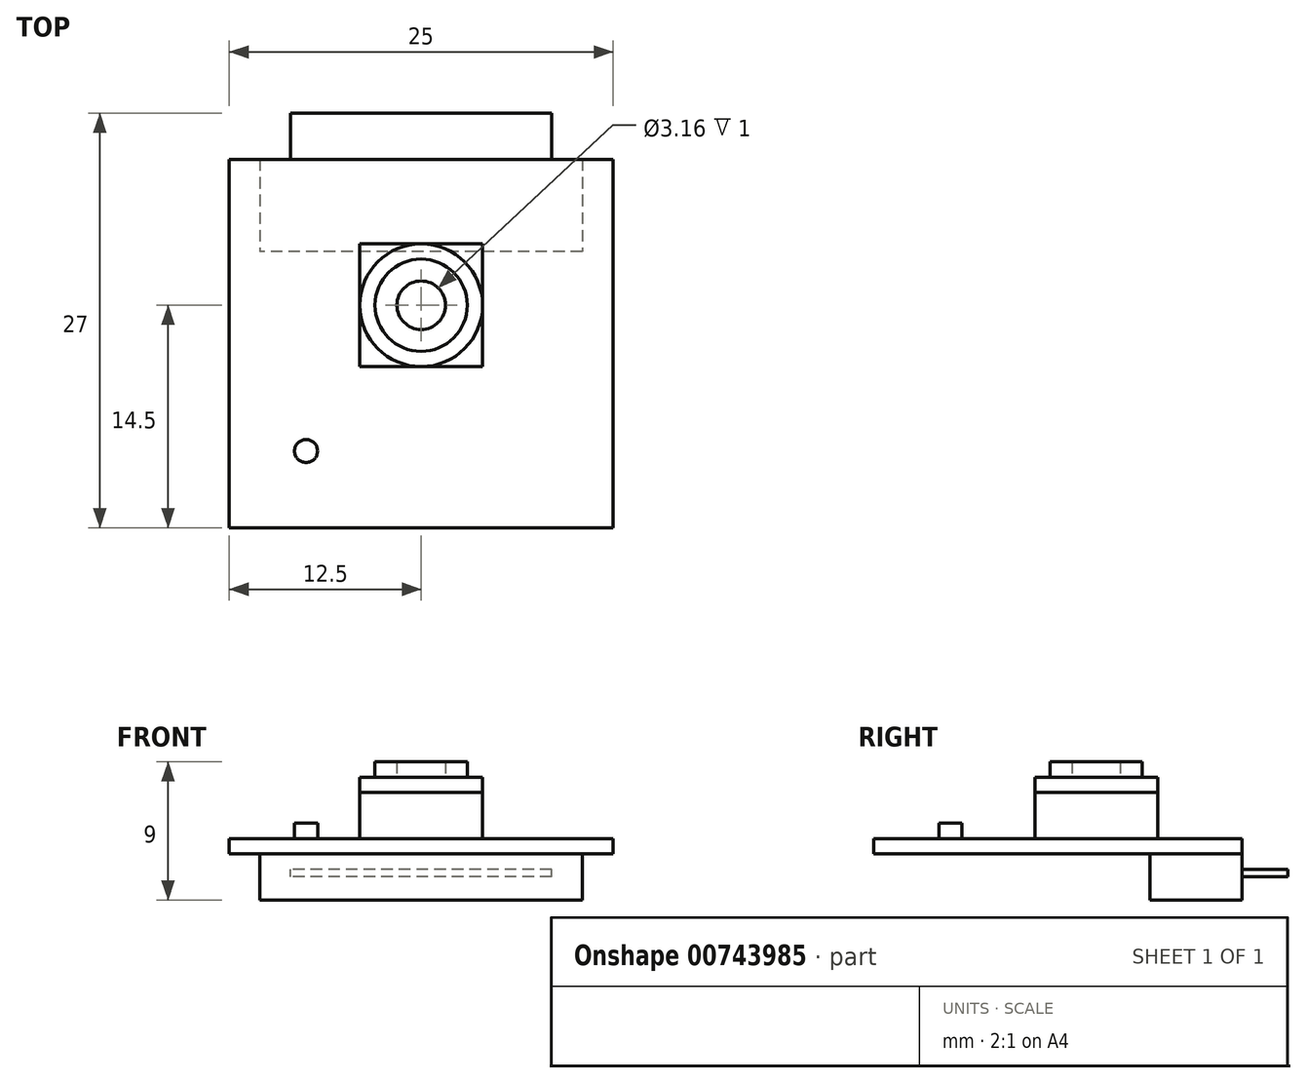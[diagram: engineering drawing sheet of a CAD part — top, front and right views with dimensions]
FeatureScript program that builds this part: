
annotation { "Feature Type Name" : "Feature", "Feature Type Description" : "" }
export const myFeature = defineFeature(function(context is Context, id is Id, definition is map)
    precondition{}
    {
        {
            var Q0;
            Q0=qCreatedBy(makeId("Top.planeOp"),FACE);
            var sketch = newSketch(context, id + "F0", { "sketchPlane" : qUnion([Q0])});
            skLineSegment(sketch, "E0", {"start": v(0, 11.87) * mm, "end": v(0, -10.8) * mm, "construction": true});
            skLineSegment(sketch, "E1", {"start": v(-15.08, 0) * mm, "end": v(17.29, 0) * mm, "construction": true});
            skLineSegment(sketch, "E2.bottom", {"start": v(-12.5, 12) * mm, "end": v(12.5, 12) * mm});
            skLineSegment(sketch, "E2.top", {"start": v(-12.5, -12) * mm, "end": v(12.5, -12) * mm});
            skLineSegment(sketch, "E2.left", {"start": v(-12.5, 12) * mm, "end": v(-12.5, -12) * mm});
            skLineSegment(sketch, "E2.right", {"start": v(12.5, 12) * mm, "end": v(12.5, -12) * mm});
            skSolve(sketch);
        }
        {
            var Q0;
            Q0=makeQuery(id+"F0.imprint","IMPRINT",FACE,{"disambiguationData":[TD([[makeQuery(id+"F0.imprint","IMPRINT",EDGE,{"derivedFrom":sQuery(id+"F0.wireOp",EDGE,"E2.bottom")}),-1.0]])]});
            extrude(context, id + "F1", {"entities" : qUnion([Q0]), "depth" : 1 * mm, "offsetDistance" : 25 * mm});
        }
        {
            var Q0;
            Q0=makeQuery(id+"F1.opExtrude","CAP_FACE",FACE,{"disambiguationData":[OSD([sQuery(id+"F0.wireOp",EDGE,"E2.bottom"),sQuery(id+"F0.wireOp",EDGE,"E2.top"),sQuery(id+"F0.wireOp",EDGE,"E2.left"),sQuery(id+"F0.wireOp",EDGE,"E2.right")])],"isStart":false});
            var sketch = newSketch(context, id + "F2", { "sketchPlane" : qUnion([Q0])});
            skLineSegment(sketch, "E3", {"start": v(0, 13.16) * mm, "end": v(0, -11.99) * mm, "construction": true});
            skLineSegment(sketch, "E4", {"start": v(-18.25, 0) * mm, "end": v(20.47, 0) * mm, "construction": true});
            skLineSegment(sketch, "E5.bottom", {"start": v(-4, 6.5) * mm, "end": v(4, 6.5) * mm});
            skLineSegment(sketch, "E5.top", {"start": v(-4, -1.5) * mm, "end": v(4, -1.5) * mm});
            skLineSegment(sketch, "E5.left", {"start": v(-4, 6.5) * mm, "end": v(-4, -1.5) * mm});
            skLineSegment(sketch, "E5.right", {"start": v(4, 6.5) * mm, "end": v(4, -1.5) * mm});
            skPoint(sketch, "E6", {"position": v(-7.5, -7) * mm});
            skCircle(sketch, "E7", {"center": v(-7.5, -7) * mm, "radius": 0.75 * mm});
            skSolve(sketch);
        }
        {
            var Q0;
            Q0=makeQuery(id+"F2.imprint","IMPRINT",FACE,{"disambiguationData":[TD([[makeQuery(id+"F2.imprint","IMPRINT",EDGE,{"derivedFrom":sQuery(id+"F2.wireOp",EDGE,"E5.bottom")}),-1.0]])]});
            extrude(context, id + "F3", {"entities" : qUnion([Q0]), "operationType" : NewBodyOperationType.ADD, "depth" : 4 * mm, "offsetDistance" : 25 * mm});
        }
        {
            var Q0;
            Q0=makeQuery(id+"F3.opExtrude","CAP_FACE",FACE,{"disambiguationData":[OSD([sQuery(id+"F2.wireOp",EDGE,"E5.bottom"),sQuery(id+"F2.wireOp",EDGE,"E5.top"),sQuery(id+"F2.wireOp",EDGE,"E5.left"),sQuery(id+"F2.wireOp",EDGE,"E5.right")])],"isStart":false});
            var sketch = newSketch(context, id + "F4", { "sketchPlane" : qUnion([Q0])});
            skCircle(sketch, "E8", {"center": v(0, 2.5) * mm, "radius": 4 * mm});
            skSolve(sketch);
        }
        {
            var Q0;
            {var subQ0=sQuery(id+"F4.wireOp",EDGE,"E8");var subQ1=makeQuery(id+"F3.opExtrude","CAP_EDGE",EDGE,{"disambiguationData":[OSD([sQuery(id+"F2.wireOp",EDGE,"E5.bottom")])],"isStart":false});var subQ2=makeQuery(id+"F4.imprint","INTERSECT",VERTEX,{"derivedFrom":[subQ1,subQ0]});Q0=makeQuery(id+"F4.imprint","IMPRINT",FACE,{"disambiguationData":[TD([[makeQuery(id+"F4.imprint","IMPRINT",EDGE,{"disambiguationData":[TD([[subQ2,1.0]])],"derivedFrom":subQ0}),-1.0]])]});}
            var Q1;
            {var subQ0=sQuery(id+"F4.wireOp",EDGE,"E8");var subQ1=makeQuery(id+"F3.opExtrude","CAP_EDGE",EDGE,{"disambiguationData":[OSD([sQuery(id+"F2.wireOp",EDGE,"E5.bottom")])],"isStart":false});var subQ2=makeQuery(id+"F4.imprint","INTERSECT",VERTEX,{"derivedFrom":[subQ1,subQ0]});Q1=makeQuery(id+"F4.imprint","IMPRINT",FACE,{"disambiguationData":[TD([[makeQuery(id+"F4.imprint","IMPRINT",EDGE,{"disambiguationData":[TD([[subQ2,-1.0]])],"derivedFrom":subQ0}),-1.0]])]});}
            var Q2;
            {var subQ0=sQuery(id+"F4.wireOp",EDGE,"E8");var subQ1=makeQuery(id+"F3.opExtrude","CAP_EDGE",EDGE,{"disambiguationData":[OSD([sQuery(id+"F2.wireOp",EDGE,"E5.left")])],"isStart":false});var subQ2=makeQuery(id+"F4.imprint","INTERSECT",VERTEX,{"derivedFrom":[subQ1,subQ0]});Q2=makeQuery(id+"F4.imprint","IMPRINT",FACE,{"disambiguationData":[TD([[makeQuery(id+"F4.imprint","IMPRINT",EDGE,{"disambiguationData":[TD([[subQ2,-1.0]])],"derivedFrom":subQ0}),-1.0]])]});}
            var Q3;
            {var subQ0=sQuery(id+"F4.wireOp",EDGE,"E8");var subQ1=makeQuery(id+"F3.opExtrude","CAP_EDGE",EDGE,{"disambiguationData":[OSD([sQuery(id+"F2.wireOp",EDGE,"E5.right")])],"isStart":false});var subQ2=makeQuery(id+"F4.imprint","INTERSECT",VERTEX,{"derivedFrom":[subQ1,subQ0]});Q3=makeQuery(id+"F4.imprint","IMPRINT",FACE,{"disambiguationData":[TD([[makeQuery(id+"F4.imprint","IMPRINT",EDGE,{"disambiguationData":[TD([[subQ2,1.0]])],"derivedFrom":subQ0}),-1.0]])]});}
            extrude(context, id + "F5", {"entities" : qUnion([Q0, Q1, Q2, Q3]), "operationType" : NewBodyOperationType.REMOVE, "oppositeDirection" : true, "depth" : 1 * mm, "offsetDistance" : 25 * mm});
        }
        {
            var Q0;
            Q0=makeQuery(id+"F3.opExtrude","CAP_FACE",FACE,{"disambiguationData":[OSD([sQuery(id+"F2.wireOp",EDGE,"E5.bottom"),sQuery(id+"F2.wireOp",EDGE,"E5.top"),sQuery(id+"F2.wireOp",EDGE,"E5.left"),sQuery(id+"F2.wireOp",EDGE,"E5.right")])],"isStart":false});
            var sketch = newSketch(context, id + "F6", { "sketchPlane" : qUnion([Q0])});
            skCircle(sketch, "E9", {"center": v(0, 2.5) * mm, "radius": 3 * mm});
            skCircle(sketch, "E10", {"center": v(0, 2.5) * mm, "radius": 1.58 * mm});
            skSolve(sketch);
        }
        {
            var Q0;
            Q0=makeQuery(id+"F6.imprint","IMPRINT",FACE,{"disambiguationData":[TD([[makeQuery(id+"F6.imprint","IMPRINT",EDGE,{"derivedFrom":sQuery(id+"F6.wireOp",EDGE,"E9")}),1.0]])]});
            extrude(context, id + "F7", {"entities" : qUnion([Q0]), "operationType" : NewBodyOperationType.ADD, "depth" : 1 * mm, "offsetDistance" : 25 * mm});
        }
        {
            var Q0;
            Q0=makeQuery(id+"F1.opExtrude","CAP_FACE",FACE,{"disambiguationData":[OSD([sQuery(id+"F0.wireOp",EDGE,"E2.bottom"),sQuery(id+"F0.wireOp",EDGE,"E2.top"),sQuery(id+"F0.wireOp",EDGE,"E2.left"),sQuery(id+"F0.wireOp",EDGE,"E2.right")])],"isStart":true});
            var sketch = newSketch(context, id + "F8", { "sketchPlane" : qUnion([Q0])});
            skLineSegment(sketch, "E11.bottom", {"start": v(10.5, -12) * mm, "end": v(-10.5, -12) * mm});
            skLineSegment(sketch, "E11.top", {"start": v(10.5, -6) * mm, "end": v(-10.5, -6) * mm});
            skLineSegment(sketch, "E11.left", {"start": v(10.5, -12) * mm, "end": v(10.5, -6) * mm});
            skLineSegment(sketch, "E11.right", {"start": v(-10.5, -12) * mm, "end": v(-10.5, -6) * mm});
            skSolve(sketch);
        }
        {
            var Q0;
            Q0=makeQuery(id+"F8.imprint","IMPRINT",FACE,{"disambiguationData":[TD([[makeQuery(id+"F8.imprint","IMPRINT",EDGE,{"derivedFrom":sQuery(id+"F8.wireOp",EDGE,"E11.bottom")}),1.0]])]});
            extrude(context, id + "F9", {"entities" : qUnion([Q0]), "operationType" : NewBodyOperationType.ADD, "depth" : 3 * mm, "offsetDistance" : 25 * mm});
        }
        {
            var Q0;
            Q0=makeQuery(id+"F9.boolean.opBoolean","MERGE",FACE,{"derivedFrom":[makeQuery(id+"F1.opExtrude","SWEPT_FACE",FACE,{"disambiguationData":[OSD([sQuery(id+"F0.wireOp",EDGE,"E2.bottom")])]}),makeQuery(id+"F9.opExtrude","SWEPT_FACE",FACE,{"disambiguationData":[OSD([sQuery(id+"F8.wireOp",EDGE,"E11.bottom")])]})]});
            var sketch = newSketch(context, id + "F10", { "sketchPlane" : qUnion([Q0])});
            skLineSegment(sketch, "E12.bottom", {"start": v(-8.5, -1.5) * mm, "end": v(8.5, -1.5) * mm});
            skLineSegment(sketch, "E12.top", {"start": v(-8.5, -1) * mm, "end": v(8.5, -1) * mm});
            skLineSegment(sketch, "E12.left", {"start": v(-8.5, -1.5) * mm, "end": v(-8.5, -1) * mm});
            skLineSegment(sketch, "E12.right", {"start": v(8.5, -1.5) * mm, "end": v(8.5, -1) * mm});
            skSolve(sketch);
        }
        {
            var Q0;
            Q0=makeQuery(id+"F10.imprint","IMPRINT",FACE,{"disambiguationData":[TD([[makeQuery(id+"F10.imprint","IMPRINT",EDGE,{"derivedFrom":sQuery(id+"F10.wireOp",EDGE,"E12.bottom")}),1.0]])]});
            extrude(context, id + "F11", {"entities" : qUnion([Q0]), "operationType" : NewBodyOperationType.ADD, "depth" : 3 * mm, "offsetDistance" : 25 * mm});
        }
        {
            var Q0;
            Q0=makeQuery(id+"F2.imprint","IMPRINT",FACE,{"disambiguationData":[TD([[makeQuery(id+"F2.imprint","IMPRINT",EDGE,{"derivedFrom":sQuery(id+"F2.wireOp",EDGE,"E7")}),1.0]])]});
            extrude(context, id + "F12", {"entities" : qUnion([Q0]), "operationType" : NewBodyOperationType.ADD, "depth" : 1 * mm, "offsetDistance" : 25 * mm});
        }
    });
